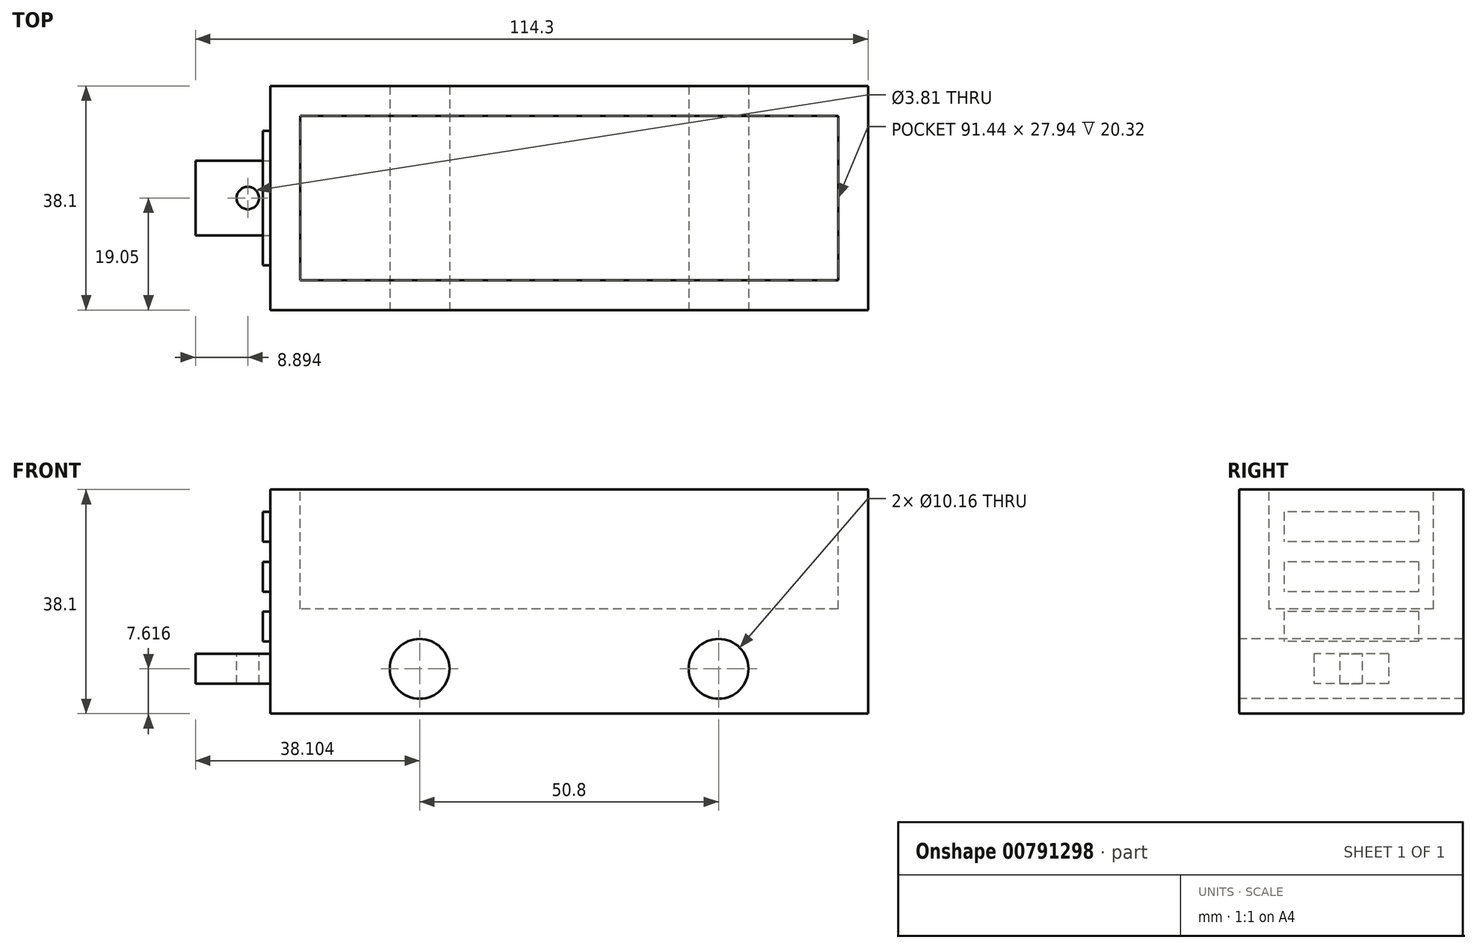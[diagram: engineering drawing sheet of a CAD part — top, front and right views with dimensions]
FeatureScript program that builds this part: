
annotation { "Feature Type Name" : "Feature", "Feature Type Description" : "" }
export const myFeature = defineFeature(function(context is Context, id is Id, definition is map)
    precondition{}
    {
        {
            var Q0;
            Q0=qCreatedBy(makeId("Front.planeOp"),FACE);
            var sketch = newSketch(context, id + "F0", { "sketchPlane" : qUnion([Q0])});
            skLineSegment(sketch, "E0.bottom", {"start": v(-53.18, 18.59) * mm, "end": v(48.42, 18.59) * mm});
            skLineSegment(sketch, "E0.top", {"start": v(-53.18, -19.51) * mm, "end": v(48.42, -19.51) * mm});
            skLineSegment(sketch, "E0.left", {"start": v(-53.18, 18.59) * mm, "end": v(-53.18, -19.51) * mm});
            skLineSegment(sketch, "E0.right", {"start": v(48.42, 18.59) * mm, "end": v(48.42, -19.51) * mm});
            skSolve(sketch);
        }
        {
            var Q0;
            Q0=qSketchRegion(id+"F0",true);
            extrude(context, id + "F1", {"entities" : qUnion([Q0]), "depth" : 38.1 * mm});
        }
        {
            var Q0;
            Q0=makeQuery(id+"F1.opExtrude","SWEPT_FACE",FACE,{"disambiguationData":[OSD([sQuery(id+"F0.wireOp",EDGE,"E0.bottom")])]});
            var sketch = newSketch(context, id + "F2", { "sketchPlane" : qUnion([Q0])});
            skLineSegment(sketch, "E1.bottom", {"start": v(43.34, -5.08) * mm, "end": v(-48.1, -5.08) * mm});
            skLineSegment(sketch, "E1.top", {"start": v(43.34, -33.02) * mm, "end": v(-48.1, -33.02) * mm});
            skLineSegment(sketch, "E1.left", {"start": v(43.34, -5.08) * mm, "end": v(43.34, -33.02) * mm});
            skLineSegment(sketch, "E1.right", {"start": v(-48.1, -5.08) * mm, "end": v(-48.1, -33.02) * mm});
            skSolve(sketch);
        }
        {
            var Q0;
            Q0=makeQuery(id+"F2.imprint","IMPRINT",FACE,{"disambiguationData":[TD([[makeQuery(id+"F2.imprint","IMPRINT",EDGE,{"derivedFrom":sQuery(id+"F2.wireOp",EDGE,"E1.bottom")}),1.0]])]});
            extrude(context, id + "F3", {"entities" : qUnion([Q0]), "operationType" : NewBodyOperationType.REMOVE, "oppositeDirection" : true, "depth" : 20.32 * mm});
        }
        {
            var Q0;
            Q0=makeQuery(id+"F1.opExtrude","CAP_FACE",FACE,{"disambiguationData":[OSD([sQuery(id+"F0.wireOp",EDGE,"E0.bottom"),sQuery(id+"F0.wireOp",EDGE,"E0.top"),sQuery(id+"F0.wireOp",EDGE,"E0.left"),sQuery(id+"F0.wireOp",EDGE,"E0.right")])],"isStart":false});
            var sketch = newSketch(context, id + "F4", { "sketchPlane" : qUnion([Q0])});
            skCircle(sketch, "E2", {"center": v(-27.78, -11.9) * mm, "radius": 5.08 * mm});
            skCircle(sketch, "E3", {"center": v(23.02, -11.9) * mm, "radius": 5.08 * mm});
            skSolve(sketch);
        }
        {
            var Q0;
            Q0=makeQuery(id+"F4.imprint","IMPRINT",FACE,{"disambiguationData":[TD([[makeQuery(id+"F4.imprint","IMPRINT",EDGE,{"derivedFrom":sQuery(id+"F4.wireOp",EDGE,"E2")}),1.0]])]});
            var Q1;
            Q1=makeQuery(id+"F4.imprint","IMPRINT",FACE,{"disambiguationData":[TD([[makeQuery(id+"F4.imprint","IMPRINT",EDGE,{"derivedFrom":sQuery(id+"F4.wireOp",EDGE,"E3")}),1.0]])]});
            extrude(context, id + "F5", {"entities" : qUnion([Q0, Q1]), "operationType" : NewBodyOperationType.REMOVE, "endBound" : BoundingType.THROUGH_ALL, "oppositeDirection" : true, "depth" : 25.4 * mm});
        }
        {
            var Q0;
            Q0=makeQuery(id+"F1.opExtrude","SWEPT_FACE",FACE,{"disambiguationData":[OSD([sQuery(id+"F0.wireOp",EDGE,"E0.left")])]});
            var sketch = newSketch(context, id + "F6", { "sketchPlane" : qUnion([Q0])});
            skLineSegment(sketch, "E4.bottom", {"start": v(7.62, 14.78) * mm, "end": v(30.48, 14.78) * mm});
            skLineSegment(sketch, "E4.top", {"start": v(7.62, -15.7) * mm, "end": v(30.48, -15.7) * mm});
            skLineSegment(sketch, "E4.left", {"start": v(7.62, 14.78) * mm, "end": v(7.62, -15.7) * mm});
            skLineSegment(sketch, "E4.right", {"start": v(30.48, 14.78) * mm, "end": v(30.48, -15.7) * mm});
            skLineSegment(sketch, "E5", {"start": v(7.62, 9.7) * mm, "end": v(30.48, 9.7) * mm});
            skLineSegment(sketch, "E6", {"start": v(7.62, 6.3) * mm, "end": v(30.48, 6.3) * mm});
            skLineSegment(sketch, "E7", {"start": v(7.62, 1.23) * mm, "end": v(30.48, 1.23) * mm});
            skLineSegment(sketch, "E8", {"start": v(7.62, -2.15) * mm, "end": v(30.48, -2.15) * mm});
            skLineSegment(sketch, "E9", {"start": v(7.62, -7.23) * mm, "end": v(30.48, -7.23) * mm});
            skLineSegment(sketch, "E10", {"start": v(7.62, -10.6) * mm, "end": v(30.48, -10.6) * mm});
            skSolve(sketch);
        }
        {
            var Q0;
            {var subQ0=sQuery(id+"F6.wireOp",EDGE,"E4.bottom");Q0=makeQuery(id+"F6.imprint","IMPRINT",FACE,{"disambiguationData":[TD([[makeQuery(id+"F6.imprint","IMPRINT",EDGE,{"derivedFrom":subQ0}),-1.0]])]});}
            var Q1;
            {var subQ0=sQuery(id+"F6.wireOp",EDGE,"E6");Q1=makeQuery(id+"F6.imprint","IMPRINT",FACE,{"disambiguationData":[TD([[makeQuery(id+"F6.imprint","IMPRINT",EDGE,{"derivedFrom":subQ0}),-1.0]])]});}
            var Q2;
            {var subQ0=sQuery(id+"F6.wireOp",EDGE,"E8");Q2=makeQuery(id+"F6.imprint","IMPRINT",FACE,{"disambiguationData":[TD([[makeQuery(id+"F6.imprint","IMPRINT",EDGE,{"derivedFrom":subQ0}),-1.0]])]});}
            extrude(context, id + "F7", {"entities" : qUnion([Q0, Q1, Q2]), "operationType" : NewBodyOperationType.ADD, "depth" : 1.27 * mm});
        }
        {
            var Q0;
            Q0=makeQuery(id+"F1.opExtrude","SWEPT_FACE",FACE,{"disambiguationData":[OSD([sQuery(id+"F0.wireOp",EDGE,"E0.left")])]});
            var sketch = newSketch(context, id + "F8", { "sketchPlane" : qUnion([Q0])});
            skLineSegment(sketch, "E11.bottom", {"start": v(12.7, -9.35) * mm, "end": v(25.4, -9.35) * mm});
            skLineSegment(sketch, "E11.top", {"start": v(12.7, -14.43) * mm, "end": v(25.4, -14.43) * mm});
            skLineSegment(sketch, "E11.left", {"start": v(12.7, -9.35) * mm, "end": v(12.7, -14.43) * mm});
            skLineSegment(sketch, "E11.right", {"start": v(25.4, -9.35) * mm, "end": v(25.4, -14.43) * mm});
            skSolve(sketch);
        }
        {
            var Q0;
            Q0=qSketchRegion(id+"F8",true);
            extrude(context, id + "F9", {"entities" : qUnion([Q0]), "operationType" : NewBodyOperationType.ADD, "depth" : 12.7 * mm});
        }
        {
            var Q0;
            Q0=makeQuery(id+"F9.opExtrude","SWEPT_FACE",FACE,{"disambiguationData":[OSD([sQuery(id+"F8.wireOp",EDGE,"E11.bottom")])]});
            var sketch = newSketch(context, id + "F10", { "sketchPlane" : qUnion([Q0])});
            skCircle(sketch, "E12", {"center": v(-56.99, -19.05) * mm, "radius": 1.9 * mm});
            skSolve(sketch);
        }
        {
            var Q0;
            Q0=makeQuery(id+"F10.imprint","IMPRINT",FACE,{"disambiguationData":[TD([[makeQuery(id+"F10.imprint","IMPRINT",EDGE,{"derivedFrom":sQuery(id+"F10.wireOp",EDGE,"E12")}),1.0]])]});
            extrude(context, id + "F11", {"entities" : qUnion([Q0]), "operationType" : NewBodyOperationType.REMOVE, "endBound" : BoundingType.THROUGH_ALL, "oppositeDirection" : true, "depth" : 25.4 * mm});
        }
    });
